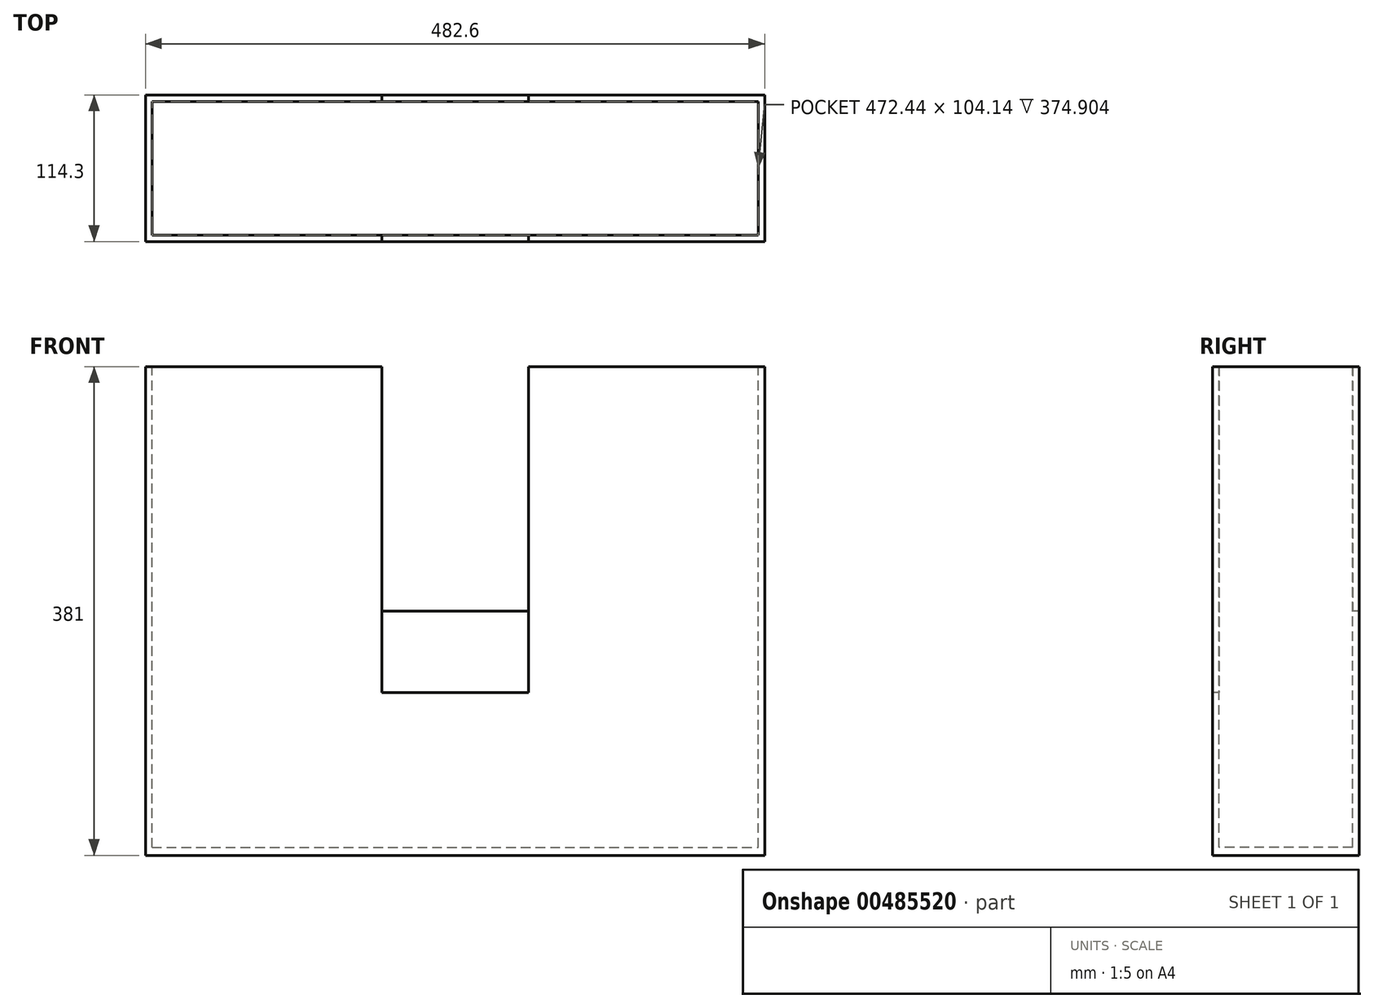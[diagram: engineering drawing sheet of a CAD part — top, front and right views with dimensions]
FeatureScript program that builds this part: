
annotation { "Feature Type Name" : "Feature", "Feature Type Description" : "" }
export const myFeature = defineFeature(function(context is Context, id is Id, definition is map)
    precondition{}
    {
        {
            var Q0;
            Q0=qCreatedBy(makeId("Front.planeOp"),FACE);
            var sketch = newSketch(context, id + "F0", { "sketchPlane" : qUnion([Q0])});
            skLineSegment(sketch, "E0.bottom", {"start": v(241.3, -190.5) * mm, "end": v(-241.3, -190.5) * mm});
            skLineSegment(sketch, "E0.top", {"start": v(241.3, 190.5) * mm, "end": v(57.15, 190.5) * mm});
            skLineSegment(sketch, "E0.left", {"start": v(241.3, -190.5) * mm, "end": v(241.3, 190.5) * mm});
            skLineSegment(sketch, "E0.right", {"start": v(-241.3, -190.5) * mm, "end": v(-241.3, 190.5) * mm});
            skPoint(sketch, "E0.middle", {"position": v(0, 0) * mm});
            skLineSegment(sketch, "E1.bottom", {"start": v(57.15, 0) * mm, "end": v(-57.15, 0) * mm});
            skLineSegment(sketch, "E1.top", {"start": v(57.15, 0) * mm, "end": v(-57.15, 0) * mm});
            skLineSegment(sketch, "E1.left", {"start": v(57.15, 0) * mm, "end": v(57.15, 0) * mm});
            skLineSegment(sketch, "E1.right", {"start": v(-57.15, 0) * mm, "end": v(-57.15, 0) * mm});
            skLineSegment(sketch, "E2", {"start": v(-57.15, 0) * mm, "end": v(-57.15, 190.5) * mm});
            skLineSegment(sketch, "E3", {"start": v(57.15, 0) * mm, "end": v(57.15, 190.5) * mm});
            skLineSegment(sketch, "E4.trimOffspring", {"start": v(-57.15, 190.5) * mm, "end": v(-241.3, 190.5) * mm});
            skSolve(sketch);
        }
        {
            var Q0;
            Q0 = qSketchRegion(id + "F0", true);
            extrude(context, id + "F1", {"entities" : qUnion([Q0]), "oppositeDirection" : true, "depth" : 114.3 * mm});
        }
        {
            var Q0;
            Q0=makeQuery(id+"F1.opExtrude","SWEPT_FACE",FACE,{"disambiguationData":[OSD([sQuery(id+"F0.wireOp",EDGE,"E4.trimOffspring")])]});
            var sketch = newSketch(context, id + "F2", { "sketchPlane" : qUnion([Q0])});
            skLineSegment(sketch, "E5", {"start": v(-236.22, 109.22) * mm, "end": v(-236.22, 5.08) * mm});
            skLineSegment(sketch, "E6", {"start": v(-236.22, 109.22) * mm, "end": v(236.22, 109.22) * mm});
            skLineSegment(sketch, "E7", {"start": v(236.22, 109.22) * mm, "end": v(236.22, 5.08) * mm});
            skLineSegment(sketch, "E8", {"start": v(-236.22, 5.08) * mm, "end": v(236.22, 5.08) * mm});
            skPoint(sketch, "E9.orphan", {"position": v(236.22, 0) * mm});
            skPoint(sketch, "E10.orphan", {"position": v(-236.22, 0) * mm});
            skSolve(sketch);
        }
        {
            var Q0;
            Q0 = qSketchRegion(id + "F2", true);
            extrude(context, id + "F3", {"entities" : qUnion([Q0]), "operationType" : NewBodyOperationType.REMOVE, "oppositeDirection" : true, "depth" : 374.9 * mm});
        }
        {
            var Q0;
            Q0=makeQuery(id+"F1.opExtrude","CAP_FACE",FACE,{"disambiguationData":[OSD([sQuery(id+"F0.wireOp",EDGE,"E0.bottom"),sQuery(id+"F0.wireOp",EDGE,"E0.top"),sQuery(id+"F0.wireOp",EDGE,"E0.left"),sQuery(id+"F0.wireOp",EDGE,"E0.right"),sQuery(id+"F0.wireOp",EDGE,"E1.top"),sQuery(id+"F0.wireOp",EDGE,"E2"),sQuery(id+"F0.wireOp",EDGE,"E3"),sQuery(id+"F0.wireOp",EDGE,"E4.trimOffspring")])],"isStart":true});
            var sketch = newSketch(context, id + "F4", { "sketchPlane" : qUnion([Q0])});
            skLineSegment(sketch, "E11", {"start": v(-57.15, 0) * mm, "end": v(-57.15, -63.5) * mm});
            skLineSegment(sketch, "E12", {"start": v(-57.15, -63.5) * mm, "end": v(57.15, -63.5) * mm});
            skLineSegment(sketch, "E13", {"start": v(57.15, -63.5) * mm, "end": v(57.15, 0) * mm});
            skLineSegment(sketch, "E14", {"start": v(57.15, 0) * mm, "end": v(-57.15, 0) * mm});
            skSolve(sketch);
        }
        {
            var Q0;
            Q0 = qSketchRegion(id + "F4", true);
            extrude(context, id + "F5", {"entities" : qUnion([Q0]), "operationType" : NewBodyOperationType.REMOVE, "oppositeDirection" : true, "depth" : 25.4 * mm});
        }
    });
